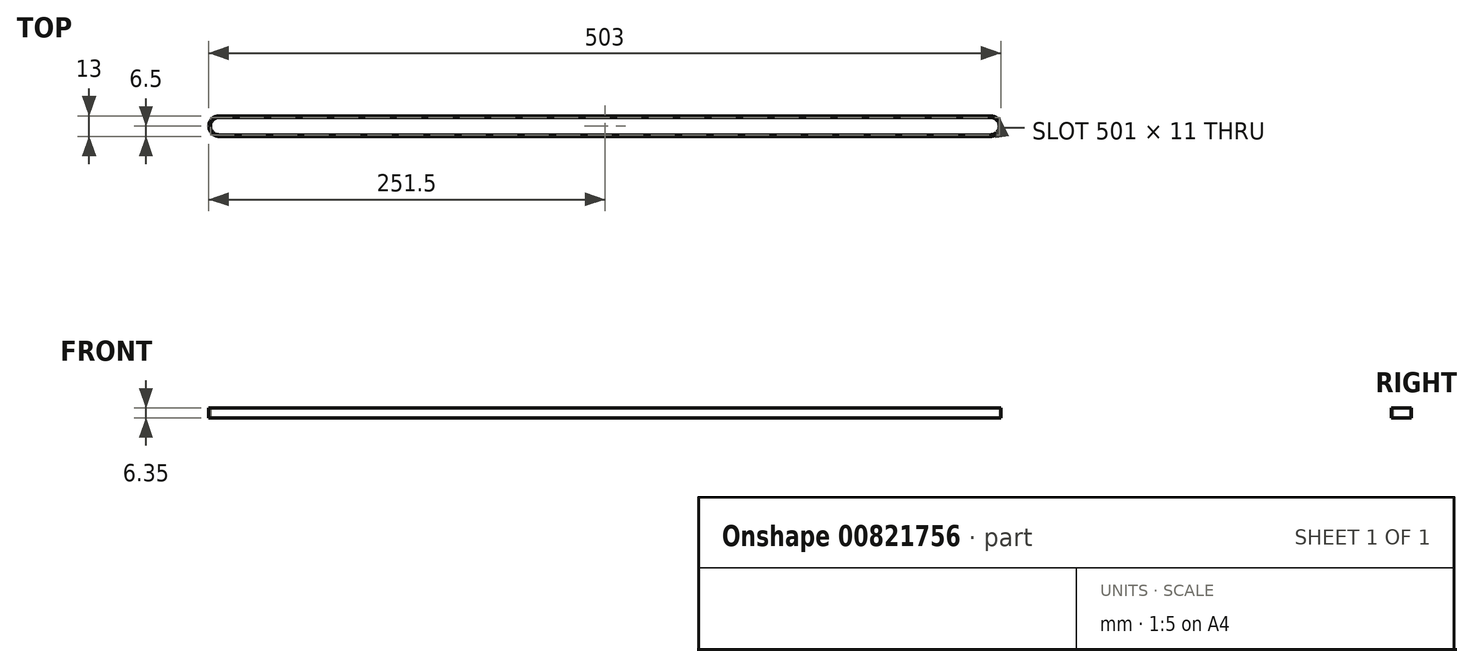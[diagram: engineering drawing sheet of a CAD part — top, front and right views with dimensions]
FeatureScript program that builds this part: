
annotation { "Feature Type Name" : "Feature", "Feature Type Description" : "" }
export const myFeature = defineFeature(function(context is Context, id is Id, definition is map)
    precondition{}
    {
        {
            var Q0;
            Q0=qCreatedBy(makeId("Top.planeOp"),FACE);
            var sketch = newSketch(context, id + "F0", { "sketchPlane" : qUnion([Q0])});
            skLineSegment(sketch, "E0.bottom", {"start": v(-245, 6.5) * mm, "end": v(245, 6.5) * mm});
            skLineSegment(sketch, "E0.top", {"start": v(-245, -6.5) * mm, "end": v(245, -6.5) * mm});
            skPoint(sketch, "E0.middle", {"position": v(0, 0) * mm});
            skArc(sketch, "E1", {"start": v(-245, 6.5) * mm, "mid": v(-251.5, 0) * mm, "end": v(-245, -6.5) * mm});
            skArc(sketch, "E2", {"start": v(245, -6.5) * mm, "mid": v(251.5, 0) * mm, "end": v(245, 6.5) * mm});
            skArc(sketch, "E3.0", {"start": v(245, -5.5) * mm, "mid": v(250.5, 0) * mm, "end": v(245, 5.5) * mm});
            skLineSegment(sketch, "E3.1", {"start": v(-245, -5.5) * mm, "end": v(245, -5.5) * mm});
            skArc(sketch, "E3.2", {"start": v(-245, 5.5) * mm, "mid": v(-250.5, 0) * mm, "end": v(-245, -5.5) * mm});
            skLineSegment(sketch, "E3.3", {"start": v(-245, 5.5) * mm, "end": v(245, 5.5) * mm});
            skSolve(sketch);
        }
        {
            var Q0;
            Q0=qSketchRegion(id+"F0",true);
            extrude(context, id + "F1", {"entities" : qUnion([Q0]), "depth" : 6.35 * mm, "offsetDistance" : 25 * mm});
        }
    });
